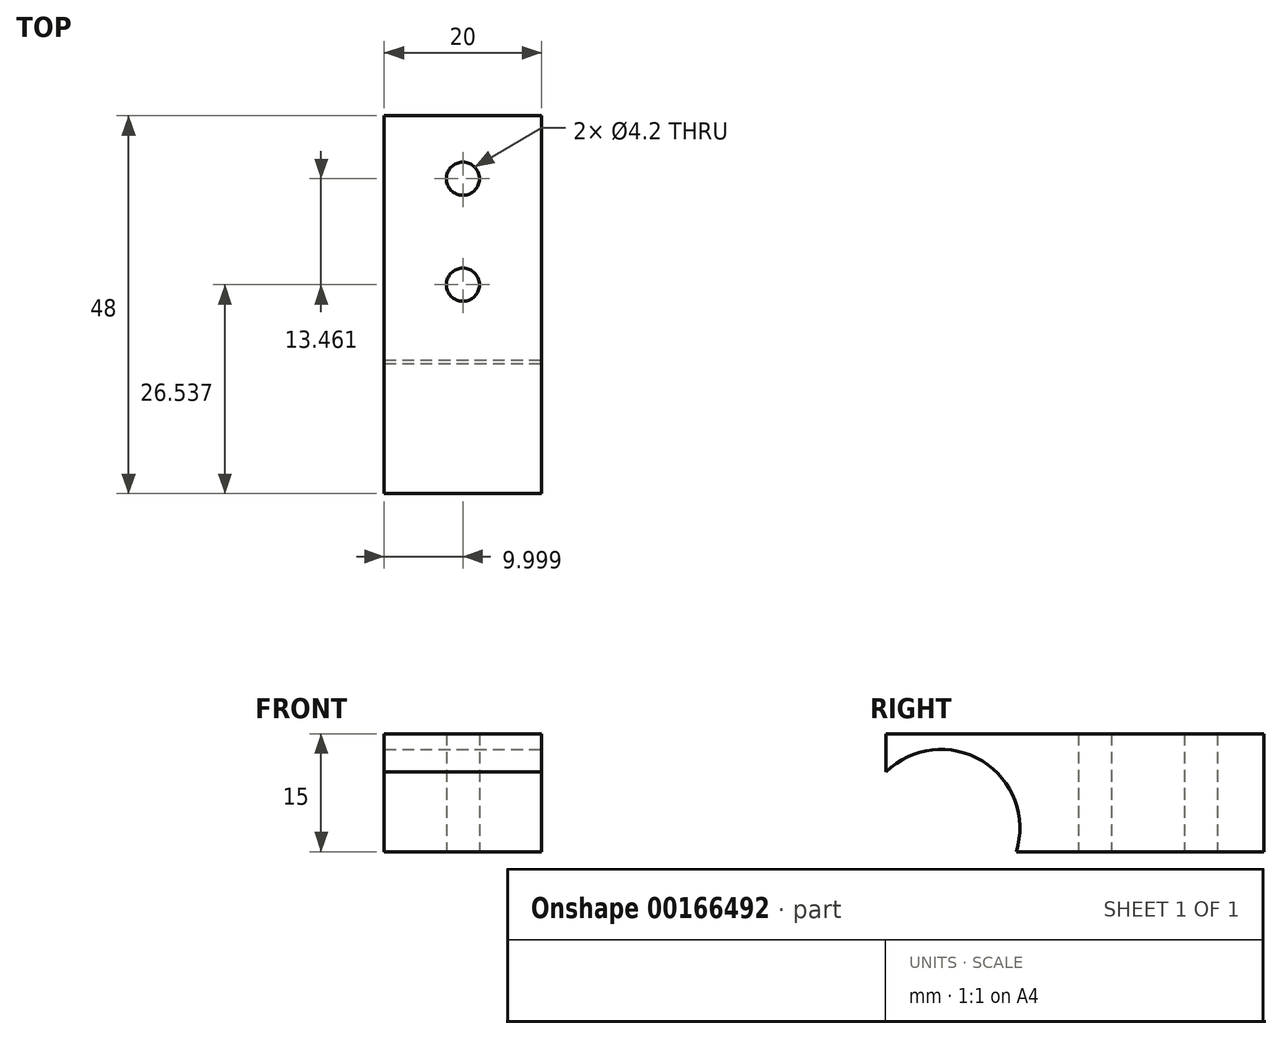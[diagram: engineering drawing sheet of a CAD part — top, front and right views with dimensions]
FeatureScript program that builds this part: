
annotation { "Feature Type Name" : "Feature", "Feature Type Description" : "" }
export const myFeature = defineFeature(function(context is Context, id is Id, definition is map)
    precondition{}
    {
        {
            var Q0;
            Q0=qCreatedBy(makeId("Top.planeOp"),FACE);
            var sketch = newSketch(context, id + "F0", { "sketchPlane" : qUnion([Q0])});
            skLineSegment(sketch, "E0.bottom", {"start": v(-3.93, -9.5) * mm, "end": v(-23.93, -9.5) * mm});
            skLineSegment(sketch, "E0.top", {"start": v(-3.93, 38.5) * mm, "end": v(-23.93, 38.5) * mm});
            skLineSegment(sketch, "E0.left", {"start": v(-3.93, -9.5) * mm, "end": v(-3.93, 38.5) * mm});
            skLineSegment(sketch, "E0.right", {"start": v(-23.93, -9.5) * mm, "end": v(-23.93, 38.5) * mm});
            skSolve(sketch);
        }
        {
            var Q0;
            Q0=makeQuery(id+"F0.imprint","IMPRINT",FACE,{"disambiguationData":[TD([[makeQuery(id+"F0.imprint","IMPRINT",EDGE,{"derivedFrom":sQuery(id+"F0.wireOp",EDGE,"E0.bottom")}),-1.0]])]});
            extrude(context, id + "F1", {"entities" : qUnion([Q0]), "depth" : 15 * mm});
        }
        {
            var Q0;
            Q0=qCreatedBy(makeId("Right.planeOp"),FACE);
            var sketch = newSketch(context, id + "F2", { "sketchPlane" : qUnion([Q0])});
            skCircle(sketch, "E1", {"center": v(-2.5, 3) * mm, "radius": 10 * mm});
            skSolve(sketch);
        }
        {
            var Q0;
            Q0=makeQuery(id+"F2.imprint","IMPRINT",FACE,{"disambiguationData":[TD([[makeQuery(id+"F2.imprint","IMPRINT",EDGE,{"derivedFrom":sQuery(id+"F2.wireOp",EDGE,"E1")}),1.0]])]});
            extrude(context, id + "F3", {"entities" : qUnion([Q0]), "operationType" : NewBodyOperationType.REMOVE, "oppositeDirection" : true, "depth" : 25 * mm});
        }
        {
            var Q0;
            Q0=makeQuery(id+"F1.opExtrude","CAP_FACE",FACE,{"disambiguationData":[OSD([sQuery(id+"F0.wireOp",EDGE,"E0.bottom"),sQuery(id+"F0.wireOp",EDGE,"E0.top"),sQuery(id+"F0.wireOp",EDGE,"E0.left"),sQuery(id+"F0.wireOp",EDGE,"E0.right")])],"isStart":true});
            var sketch = newSketch(context, id + "F4", { "sketchPlane" : qUnion([Q0])});
            skCircle(sketch, "E2", {"center": v(-13.93, -17.05) * mm, "radius": 2.1 * mm});
            skCircle(sketch, "E3", {"center": v(-13.93, -30.5) * mm, "radius": 2.1 * mm});
            skSolve(sketch);
        }
        {
            var Q0;
            Q0=makeQuery(id+"F4.imprint","IMPRINT",FACE,{"disambiguationData":[TD([[makeQuery(id+"F4.imprint","IMPRINT",EDGE,{"derivedFrom":sQuery(id+"F4.wireOp",EDGE,"E3")}),1.0]])]});
            var Q1;
            Q1=makeQuery(id+"F4.imprint","IMPRINT",FACE,{"disambiguationData":[TD([[makeQuery(id+"F4.imprint","IMPRINT",EDGE,{"derivedFrom":sQuery(id+"F4.wireOp",EDGE,"E2")}),1.0]])]});
            extrude(context, id + "F5", {"entities" : qUnion([Q0, Q1]), "operationType" : NewBodyOperationType.REMOVE, "oppositeDirection" : true, "depth" : 25 * mm});
        }
    });
